# Revit family: Umbral UM. C-1
name_source: partatom
category: Modelos genéricos
units: mm (PartAtom-declared; Revit-internal decimal feet)

## family parameters
Compartido = No
Corte con vacíos al cargar = No
Cota de conector redondo = Diámetro de uso
Puede alojar armadura = No
Punto de cálculo de habitación = No
Se basa en plano de trabajo = No
Siempre vertical = No
Tipo de pieza = Normal

## types (4) — shared parameters
Descripción = Pieza de hormigón polímero con anclaje de acero inoxidable.
Dist. entre bulones = 50 mm  [stored 0.164042 ft]
Fabricante = ULMA Architectural Solutions
Material = Hormigón polímero STONEO. Color C-1
URL = https://www.ulmaarchitectural.com
zero-valued in all types: Elevación por defecto

## per-type parameters (varying)
| type | Ancho | Ancho doble | Ancho total | Medio ancho | Modelo | Visible dos líneas | Visible una linea |
| UM15 | 150 mm | 38 mm | 175 mm  [stored 0.574147 ft] | 88 mm | Umbral UM15 | No | Sí |
| UM20 | 200 mm  [stored 0.656168 ft] | 50 mm  [stored 0.164042 ft] | 225 mm  [stored 0.738189 ft] | 113 mm | Umbral UM20 | No | Sí |
| UM25 | 250 mm  [stored 0.82021 ft] | 63 mm | 275 mm | 138 mm | Umbral UM25 | No | Sí |
| UM30 | 300 mm | 75 mm | 325 mm  [stored 1.06627 ft] | 163 mm | Umbral UM30 | Sí | No |

note: column(s) folded — value = type name in every type: Código de montaje

note: [stored X ft] marks values corroborated as IEEE doubles in the binary element streams (Revit-internal decimal feet)
